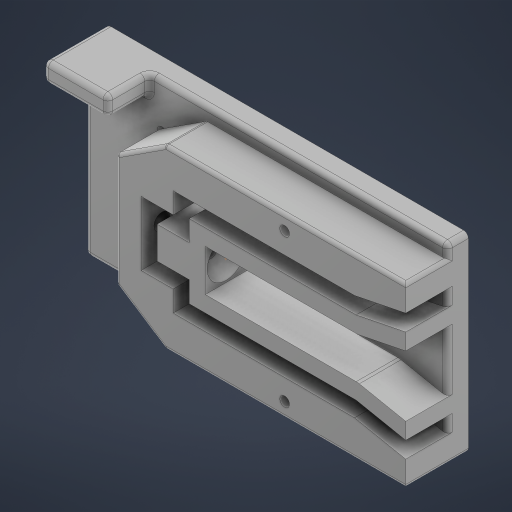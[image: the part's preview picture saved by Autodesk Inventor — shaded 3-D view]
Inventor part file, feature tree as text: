
AUTODESK INVENTOR PART (.ipt)
format: ipt  version: 2024.1 (Build 281209000, 209)  size: 4,814,848 bytes
history: native  units: mm
features: sketch x10, extrude x7, other x3, fillet x3, projected_geometry x3, plane x2, hole x2, revolve x1
ambient origin geometry x8: Origin, YZ Plane, XZ Plane, XY Plane, X Axis, Y Axis, Z Axis, Center Point
bodies: Solid1 (feature_tree)
feature tree (31):
  other  "3D_PCB1_2024-08-12"
  plane  "Work Plane1"
  extrude  "Extrusion1"  Depth=10.0mm
  extrude  "Extrusion2"  Depth=10.0mm
  extrude  "Extrusion3"  Depth=1.5mm
  fillet  "Fillet1"  Radius=1.5mm
  extrude  "Extrusion6"  Depth=1.5mm
  hole  "Hole1"  [1 undecoded]
  extrude  "Extrusion5"  TaperAngle=0.0deg  [1 undecoded]
  fillet  "Fillet2"  Radius=3.0mm
  extrude  "Extrusion7"  Depth=0.3mm
  extrude  "Extrusion8"  Depth=13.0mm
  fillet  "Fillet3"  Radius=47.5mm
  plane  "Work Plane3"
  revolve  "Revolution1"  [1 undecoded]
  hole  "Hole2"  [1 undecoded]
  sketch  "Sketch2"  dims[d0=10.0mm d1=10.0mm]
  sketch  "Sketch3"  dims[d2=10.0mm d3=10.0mm]
  sketch  "Sketch6"  dims[d4=1.5mm d5=1.5mm d6=1.5mm]
  sketch  "Sketch8"  dims[d7=1.5mm d8=1.5mm]
  sketch  "Sketch10"  dims[d9=1.5mm d10=1.5mm]
  sketch  "Sketch11"  dims[d11=3.51mm d12=0.0mm d13=0.0mm d14=3.0mm d15=0.0mm]
  sketch  "Sketch12"  dims[d19=0.3mm d20=0.3mm]
  projected_geometry  "Projected Loop4"
  sketch  "Sketch13"  dims[d21=0.3mm d22=13.0mm d23=47.5mm]
  sketch  "Sketch14"  dims[d24=3.0mm d25=5.0mm]
  other  "Work Point1"
  sketch  "Sketch17"  dims[d26=13.0mm d27=0.0mm d28=5.0mm d29=10.0mm d30=10.0mm d31=5.0mm d32=6.0mm d33=4.0mm d34=2.0mm d35=90.0deg d36=8.0mm d37=20.594885mm d41=0.0mm d42=0.0mm d43=5.0mm d44=5.0mm d46=5.0mm d49=10.0mm d50=0.0mm d52=1.0mm d53=1.0mm d54=3.0mm d55=4.0mm d56=0.0mm d57=3.0mm d58=3.0mm d59=1.0mm d60=1.0mm d61=1.0mm d62=0.5mm d63=0.5mm d64=37.718mm d65=46.0mm d66=3.0mm d67=6.0mm d68=4.0mm d69=2.0mm d70=90.0deg d71=8.0mm d72=20.594885mm d73=16.5mm d74=16.5mm d75=20.0mm d76=27.0mm d77=0.0mm d78=1.5mm d79=6.0mm d80=1.98176mm d81=1.98176mm d85=5.4mm d86=5.9mm d87=90.0deg]
  projected_geometry  "Projected Loop6"
  other  "3D_PCB1_2024-08-12.obj"
  projected_geometry  "Project Cut Edges2"
note: 4 required parameter values undecoded (feature->parameter linkage not recoverable at this tier; creation-order binding heuristic only, values carry confidence <= 0.55)